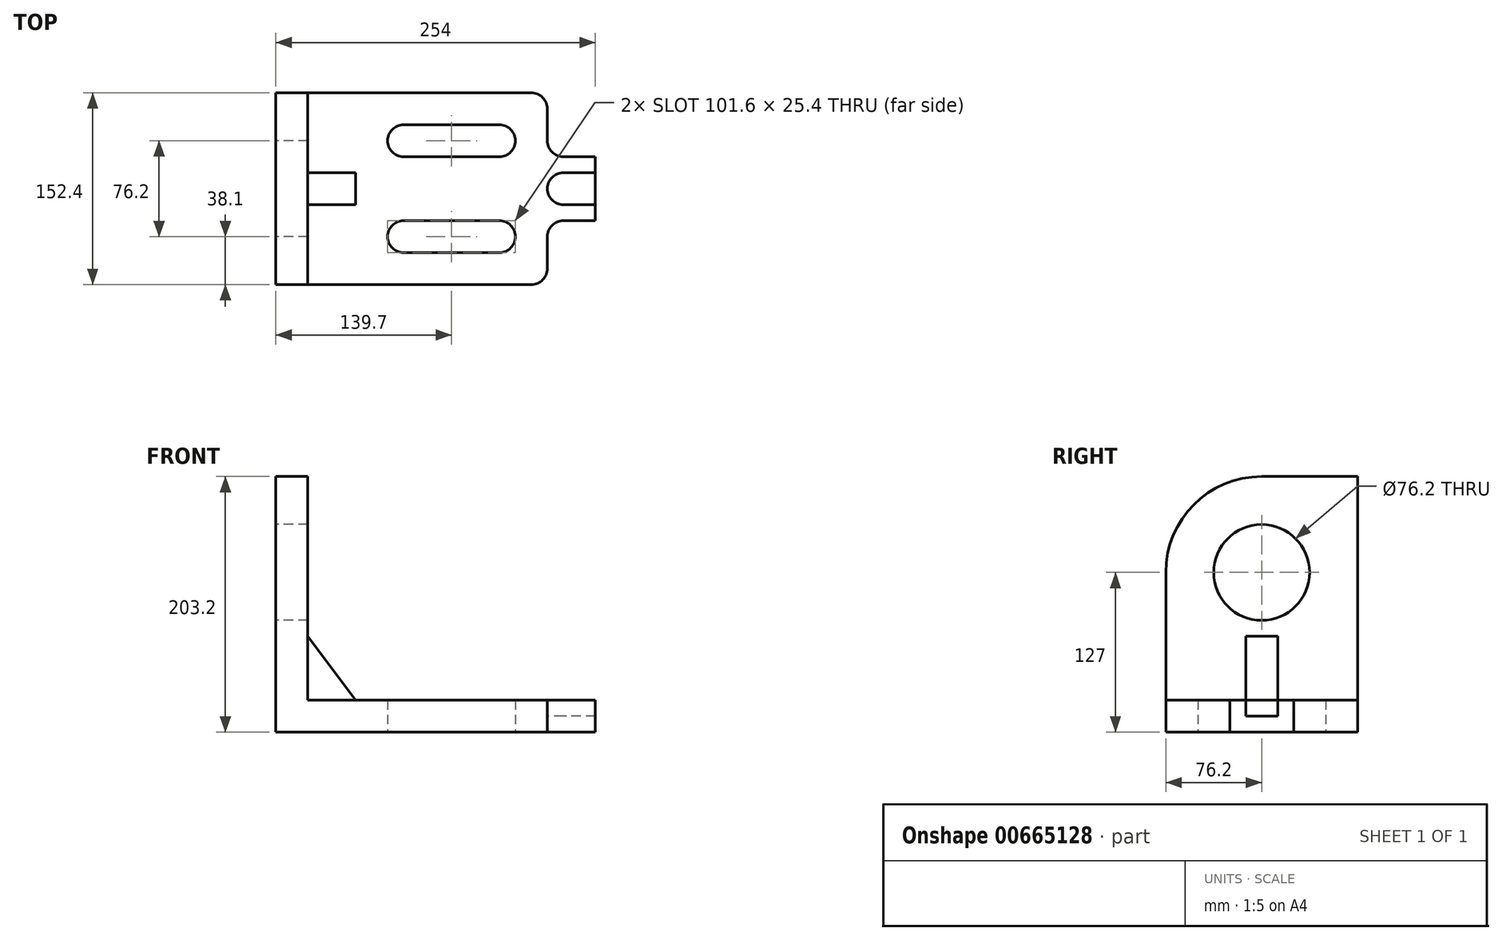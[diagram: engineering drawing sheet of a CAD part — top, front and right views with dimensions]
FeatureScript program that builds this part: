
annotation { "Feature Type Name" : "Feature", "Feature Type Description" : "" }
export const myFeature = defineFeature(function(context is Context, id is Id, definition is map)
    precondition{}
    {
        {
            var Q0;
            Q0=qCreatedBy(makeId("Top.planeOp"),FACE);
            var sketch = newSketch(context, id + "F0", { "sketchPlane" : qUnion([Q0])});
            skLineSegment(sketch, "E0", {"start": v(0, 0) * mm, "end": v(0, -152.4) * mm});
            skLineSegment(sketch, "E1", {"start": v(0, -152.4) * mm, "end": v(203.2, -152.4) * mm});
            skLineSegment(sketch, "E2", {"start": v(203.2, -152.4) * mm, "end": v(203.2, -152.4) * mm});
            skLineSegment(sketch, "E3", {"start": v(215.9, -139.7) * mm, "end": v(215.9, -114.3) * mm});
            skPoint(sketch, "E4.visualSharp", {"position": v(215.9, -152.4) * mm});
            skArc(sketch, "E4.filletArc", {"start": v(203.2, -152.4) * mm, "mid": v(212.18, -148.68) * mm, "end": v(215.9, -139.7) * mm});
            skLineSegment(sketch, "E5", {"start": v(215.9, -114.3) * mm, "end": v(215.9, -114.3) * mm});
            skLineSegment(sketch, "E6", {"start": v(228.6, -101.6) * mm, "end": v(254, -101.6) * mm});
            skLineSegment(sketch, "E7", {"start": v(254, -101.6) * mm, "end": v(254, -88.9) * mm});
            skLineSegment(sketch, "E8", {"start": v(254, -88.9) * mm, "end": v(228.6, -88.9) * mm});
            skLineSegment(sketch, "E9", {"start": v(228.6, -88.9) * mm, "end": v(228.6, -76.2) * mm});
            skLineSegment(sketch, "E10", {"start": v(228.6, -76.2) * mm, "end": v(228.6, -63.5) * mm});
            skLineSegment(sketch, "E11", {"start": v(228.6, -63.5) * mm, "end": v(254, -63.5) * mm});
            skLineSegment(sketch, "E12", {"start": v(254, -63.5) * mm, "end": v(254, -50.8) * mm});
            skLineSegment(sketch, "E13", {"start": v(254, -50.8) * mm, "end": v(228.6, -50.8) * mm});
            skLineSegment(sketch, "E14", {"start": v(215.9, -38.1) * mm, "end": v(215.9, -38.1) * mm});
            skLineSegment(sketch, "E15", {"start": v(215.9, -38.1) * mm, "end": v(215.9, -12.7) * mm});
            skLineSegment(sketch, "E16", {"start": v(203.2, 0) * mm, "end": v(203.2, 0) * mm});
            skLineSegment(sketch, "E17", {"start": v(203.2, 0) * mm, "end": v(0, 0) * mm});
            skPoint(sketch, "E18.visualSharp", {"position": v(215.9, 0) * mm});
            skArc(sketch, "E18.filletArc", {"start": v(215.9, -12.7) * mm, "mid": v(212.18, -3.72) * mm, "end": v(203.2, 0) * mm});
            skPoint(sketch, "E19.visualSharp", {"position": v(215.9, -50.8) * mm});
            skArc(sketch, "E19.filletArc", {"start": v(215.9, -38.1) * mm, "mid": v(219.62, -47.08) * mm, "end": v(228.6, -50.8) * mm});
            skPoint(sketch, "E20.visualSharp", {"position": v(215.9, -101.6) * mm});
            skArc(sketch, "E20.filletArc", {"start": v(228.6, -101.6) * mm, "mid": v(219.62, -105.32) * mm, "end": v(215.9, -114.3) * mm});
            skLineSegment(sketch, "E21", {"start": v(254, -88.9) * mm, "end": v(254, -63.5) * mm});
            skArc(sketch, "E22", {"start": v(228.6, -63.5) * mm, "mid": v(215.9, -76.2) * mm, "end": v(228.6, -88.9) * mm});
            skLineSegment(sketch, "E23", {"start": v(0, 0) * mm, "end": v(25.4, 0) * mm});
            skLineSegment(sketch, "E24", {"start": v(25.4, 0) * mm, "end": v(25.4, -63.5) * mm});
            skLineSegment(sketch, "E25", {"start": v(25.4, -63.5) * mm, "end": v(63.5, -63.5) * mm});
            skLineSegment(sketch, "E26", {"start": v(63.5, -63.5) * mm, "end": v(63.5, -88.9) * mm});
            skLineSegment(sketch, "E27", {"start": v(63.5, -88.9) * mm, "end": v(25.4, -88.9) * mm});
            skLineSegment(sketch, "E28", {"start": v(25.4, -88.9) * mm, "end": v(25.4, -152.4) * mm});
            skLineSegment(sketch, "E29", {"start": v(25.4, -63.5) * mm, "end": v(25.4, -88.9) * mm});
            skLineSegment(sketch, "E30", {"start": v(25.4, 0) * mm, "end": v(101.6, 0) * mm});
            skLineSegment(sketch, "E31", {"start": v(101.6, 0) * mm, "end": v(101.6, -38.1) * mm});
            skLineSegment(sketch, "E32", {"start": v(101.6, -38.1) * mm, "end": v(177.8, -38.1) * mm});
            skLineSegment(sketch, "E33", {"start": v(177.8, -38.1) * mm, "end": v(177.8, -25.4) * mm});
            skLineSegment(sketch, "E34", {"start": v(177.8, -25.4) * mm, "end": v(101.6, -25.4) * mm});
            skLineSegment(sketch, "E35", {"start": v(101.6, -38.1) * mm, "end": v(101.6, -50.8) * mm});
            skLineSegment(sketch, "E36", {"start": v(101.6, -50.8) * mm, "end": v(177.8, -50.8) * mm});
            skLineSegment(sketch, "E37", {"start": v(177.8, -50.8) * mm, "end": v(177.8, -38.1) * mm});
            skArc(sketch, "E38", {"start": v(101.6, -25.4) * mm, "mid": v(88.9, -38.1) * mm, "end": v(101.6, -50.8) * mm});
            skArc(sketch, "E39", {"start": v(177.8, -50.8) * mm, "mid": v(190.5, -38.1) * mm, "end": v(177.8, -25.4) * mm});
            skLineSegment(sketch, "E40", {"start": v(25.4, -152.4) * mm, "end": v(101.6, -152.4) * mm});
            skLineSegment(sketch, "E41", {"start": v(101.6, -152.4) * mm, "end": v(101.6, -114.3) * mm});
            skLineSegment(sketch, "E42", {"start": v(101.6, -114.3) * mm, "end": v(177.8, -114.3) * mm});
            skLineSegment(sketch, "E43", {"start": v(177.8, -114.3) * mm, "end": v(177.8, -127) * mm});
            skLineSegment(sketch, "E44", {"start": v(177.8, -127) * mm, "end": v(101.6, -127) * mm});
            skLineSegment(sketch, "E45", {"start": v(101.6, -114.3) * mm, "end": v(101.6, -101.6) * mm});
            skLineSegment(sketch, "E46", {"start": v(101.6, -101.6) * mm, "end": v(177.8, -101.6) * mm});
            skLineSegment(sketch, "E47", {"start": v(177.8, -101.6) * mm, "end": v(177.8, -114.3) * mm});
            skArc(sketch, "E48", {"start": v(101.6, -101.6) * mm, "mid": v(88.9, -114.3) * mm, "end": v(101.6, -127) * mm});
            skArc(sketch, "E49", {"start": v(177.8, -127) * mm, "mid": v(190.5, -114.3) * mm, "end": v(177.8, -101.6) * mm});
            skSolve(sketch);
        }
        {
            var Q0;
            {var subQ1=sQuery(id+"F0.wireOp",EDGE,"E0");Q0=makeQuery(id+"F0.imprint","IMPRINT",FACE,{"disambiguationData":[TD([[makeQuery(id+"F0.imprint","IMPRINT",EDGE,{"derivedFrom":subQ1}),1.0]])]});}
            extrude(context, id + "F1", {"entities" : qUnion([Q0]), "depth" : 203.2 * mm, "offsetDistance" : 25.4 * mm});
        }
        {
            var Q0;
            Q0=makeQuery(id+"F0.imprint","IMPRINT",FACE,{"disambiguationData":[TD([[makeQuery(id+"F0.imprint","IMPRINT",EDGE,{"derivedFrom":sQuery(id+"F0.wireOp",EDGE,"E3")}),1.0]])]});
            extrude(context, id + "F2", {"entities" : qUnion([Q0]), "operationType" : NewBodyOperationType.ADD, "depth" : 25.4 * mm, "offsetDistance" : 25.4 * mm});
        }
        {
            var Q0;
            Q0=makeQuery(id+"F0.imprint","IMPRINT",FACE,{"disambiguationData":[TD([[makeQuery(id+"F0.imprint","IMPRINT",EDGE,{"derivedFrom":sQuery(id+"F0.wireOp",EDGE,"E8")}),-1.0]])]});
            var Q1;
            Q1=makeQuery(id+"F0.imprint","IMPRINT",FACE,{"disambiguationData":[TD([[makeQuery(id+"F0.imprint","IMPRINT",EDGE,{"derivedFrom":sQuery(id+"F0.wireOp",EDGE,"E9")}),1.0]])]});
            extrude(context, id + "F3", {"entities" : qUnion([Q0, Q1]), "operationType" : NewBodyOperationType.ADD, "depth" : 12.7 * mm, "offsetDistance" : 25.4 * mm});
        }
        {
            var Q0;
            Q0=makeQuery(id+"F0.imprint","IMPRINT",FACE,{"disambiguationData":[TD([[makeQuery(id+"F0.imprint","IMPRINT",EDGE,{"derivedFrom":sQuery(id+"F0.wireOp",EDGE,"E25")}),-1.0]])]});
            extrude(context, id + "F4", {"entities" : qUnion([Q0]), "operationType" : NewBodyOperationType.ADD, "depth" : 76.2 * mm, "offsetDistance" : 25.4 * mm});
        }
        {
            var Q0;
            Q0=qCreatedBy(makeId("Right.planeOp"),FACE);
            var sketch = newSketch(context, id + "F5", { "sketchPlane" : qUnion([Q0])});
            skLineSegment(sketch, "E50", {"start": v(0, 0) * mm, "end": v(-76.2, 0) * mm});
            skLineSegment(sketch, "E51", {"start": v(-76.2, 0) * mm, "end": v(-76.2, 127) * mm});
            skSolve(sketch);
        }
        {
            var Q0;
            Q0=makeQuery(id+"F1.opExtrude","CAP_EDGE",EDGE,{"disambiguationData":[OSD([sQuery(id+"F0.wireOp",EDGE,"E1")])],"isStart":false});
            var Q1;
            Q1=makeQuery(id+"F1.opExtrude","CAP_EDGE",EDGE,{"disambiguationData":[OSD([sQuery(id+"F0.wireOp",EDGE,"E23")])],"isStart":false});
            fillet(context, id + "F6", {"entities" : qUnion([Q0, Q1]), "radius" : 76.2 * mm, "tangentPropagation" : true, "allowEdgeOverflow" : false});
        }
        {
            var Q0;
            Q0=sQuery(id+"F5.wireOp",VERTEX,"E51.end");
            var Q1;
            Q1=makeQuery(id+"F1.opExtrude","SWEPT_BODY",BODY,{"disambiguationData":[OSD([sQuery(id+"F0.wireOp",EDGE,"E0"),sQuery(id+"F0.wireOp",EDGE,"E1"),sQuery(id+"F0.wireOp",EDGE,"E23"),sQuery(id+"F0.wireOp",EDGE,"E24"),sQuery(id+"F0.wireOp",EDGE,"E28"),sQuery(id+"F0.wireOp",EDGE,"E29")])]});
            hole(context, id + "F7", {"style" : HoleStyle.SIMPLE, "endStyle" : HoleEndStyle.THROUGH, "oppositeDirection" : true, "holeDiameter" : 76.2 * mm, "majorDiameter" : 6.35 * mm, "isTappedThrough" : true, "tappedDepth" : 12.7 * mm, "tapClearance" : 3, "locations" : qUnion([Q0]), "scope" : qUnion([Q1])});
        }
        {
            var Q0;
            Q0=makeQuery(id+"F4.opExtrude","CAP_EDGE",EDGE,{"disambiguationData":[OSD([sQuery(id+"F0.wireOp",EDGE,"E26")])],"isStart":false});
            chamfer(context, id + "F8", {"entities" : qUnion([Q0]), "chamferType" : ChamferType.OFFSET_ANGLE, "width" : 50.8 * mm, "oppositeDirection" : false, "angle" : 36.87 * degree, "tangentPropagation" : true});
        }
    });
